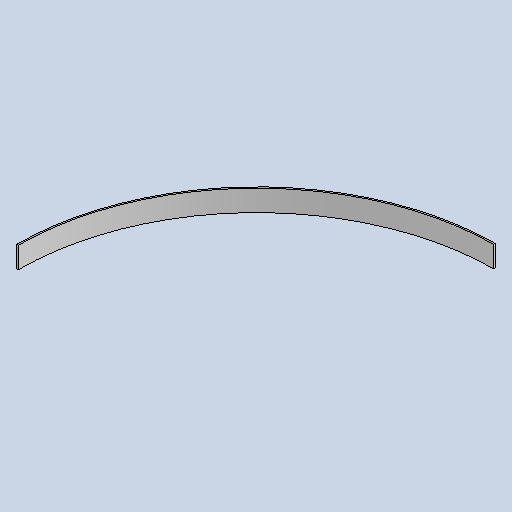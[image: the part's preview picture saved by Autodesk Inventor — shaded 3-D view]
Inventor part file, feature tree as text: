
AUTODESK INVENTOR PART (.ipt)
format: ipt  version: 2025 (Build 290162010, 162A)  size: 284,160 bytes
history: native  units: mm
features: sheet_metal_op x3, other x2, sketch x1
ambient origin geometry x8: Origin, YZ Plane, XZ Plane, XY Plane, X Axis, Y Axis, Z Axis, Center Point
bodies: Body1 (feature_tree)
feature tree (6):
  sheet_metal_op  "Contour Flange1"
  sketch  "Sketch3"  dims[d13=900.0mm d14=3.0mm d15=3.0mm d16=1.5mm d17=6.0mm d18=5.0mm d19=40.0mm d20=5.0mm d21=3.0mm d22=12.0mm d23=3.0mm d24=5.0mm d26=3.0mm]
  other  "Plate2"
  sheet_metal_op  "Bend1"
  sheet_metal_op  "Corner1"
  other  "Definition1"
